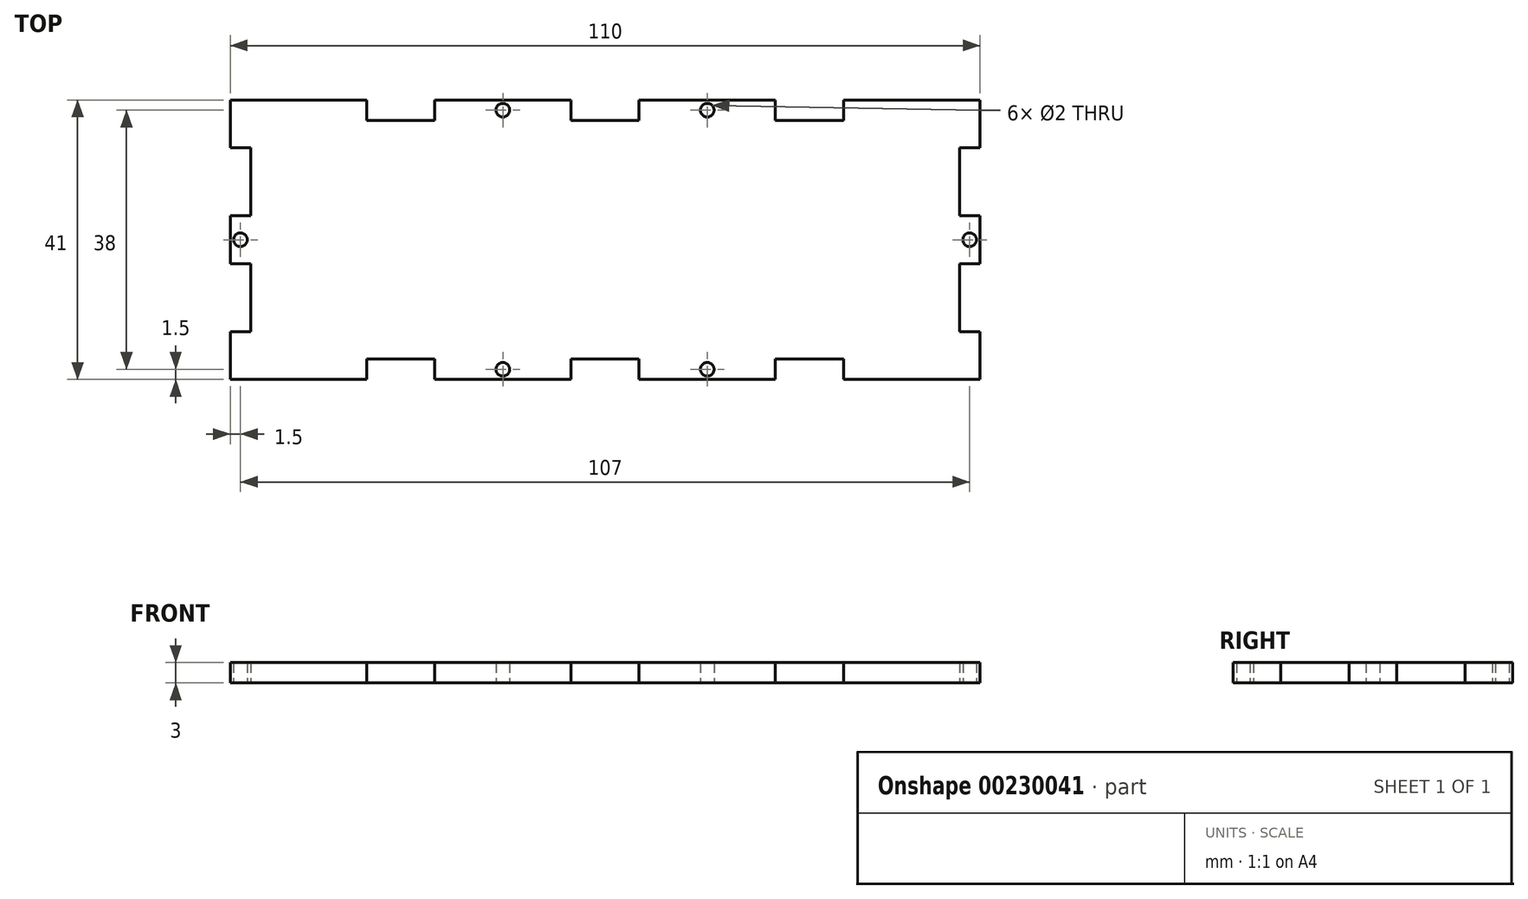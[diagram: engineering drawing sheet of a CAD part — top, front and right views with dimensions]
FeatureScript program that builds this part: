
annotation { "Feature Type Name" : "Feature", "Feature Type Description" : "" }
export const myFeature = defineFeature(function(context is Context, id is Id, definition is map)
    precondition{}
    {
        {
            var Q0;
            Q0=qCreatedBy(makeId("Top.planeOp"),FACE);
            var sketch = newSketch(context, id + "F0", { "sketchPlane" : qUnion([Q0])});
            skLineSegment(sketch, "E0", {"start": v(0, 0) * mm, "end": v(0, 7) * mm});
            skLineSegment(sketch, "E1", {"start": v(0, 7) * mm, "end": v(3, 7) * mm});
            skLineSegment(sketch, "E2", {"start": v(3, 7) * mm, "end": v(3, 17) * mm});
            skLineSegment(sketch, "E3", {"start": v(3, 17) * mm, "end": v(0, 17) * mm});
            skLineSegment(sketch, "E4", {"start": v(0, 17) * mm, "end": v(0, 24) * mm});
            skLineSegment(sketch, "E5", {"start": v(0, 24) * mm, "end": v(3, 24) * mm});
            skLineSegment(sketch, "E6", {"start": v(3, 24) * mm, "end": v(3, 34) * mm});
            skLineSegment(sketch, "E7", {"start": v(3, 34) * mm, "end": v(0, 34) * mm});
            skLineSegment(sketch, "E8", {"start": v(0, 34) * mm, "end": v(0, 41) * mm});
            skLineSegment(sketch, "E9", {"start": v(55, 41) * mm, "end": v(55, 0) * mm, "construction": true});
            skLineSegment(sketch, "E10", {"start": v(0, 20.5) * mm, "end": v(55, 20.5) * mm, "construction": true});
            skLineSegment(sketch, "E11", {"start": v(0, 41) * mm, "end": v(20, 41) * mm});
            skLineSegment(sketch, "E12", {"start": v(20, 41) * mm, "end": v(20, 38) * mm});
            skLineSegment(sketch, "E13", {"start": v(20, 38) * mm, "end": v(30, 38) * mm});
            skLineSegment(sketch, "E14", {"start": v(30, 38) * mm, "end": v(30, 41) * mm});
            skLineSegment(sketch, "E15", {"start": v(30, 41) * mm, "end": v(50, 41) * mm});
            skLineSegment(sketch, "E16", {"start": v(50, 41) * mm, "end": v(50, 38) * mm});
            skLineSegment(sketch, "E17", {"start": v(50, 38) * mm, "end": v(55, 38) * mm});
            skLineSegment(sketch, "E18.MirrorCS", {"start": v(3, 7) * mm, "end": v(0, 7) * mm});
            skLineSegment(sketch, "E19.MirrorCS", {"start": v(0, 7) * mm, "end": v(0, 0) * mm});
            skLineSegment(sketch, "E20.MirrorCS", {"start": v(0, 0) * mm, "end": v(20, 0) * mm});
            skLineSegment(sketch, "E21.MirrorCS", {"start": v(30, 0) * mm, "end": v(50, 0) * mm});
            skLineSegment(sketch, "E22.MirrorCS", {"start": v(30, 3) * mm, "end": v(30, 0) * mm});
            skLineSegment(sketch, "E23.MirrorCS", {"start": v(50, 0) * mm, "end": v(50, 3) * mm});
            skLineSegment(sketch, "E24.MirrorCS", {"start": v(50, 3) * mm, "end": v(55, 3) * mm});
            skLineSegment(sketch, "E25.MirrorCS", {"start": v(20, 0) * mm, "end": v(20, 3) * mm});
            skLineSegment(sketch, "E26.MirrorCS", {"start": v(20, 3) * mm, "end": v(30, 3) * mm});
            skCircle(sketch, "E27", {"center": v(40, 39.5) * mm, "radius": 1 * mm});
            skPoint(sketch, "E27.centerSnap0", {"position": v(50, 39.5) * mm});
            skPoint(sketch, "E27.centerSnap1", {"position": v(40, 41) * mm});
            skCircle(sketch, "E28.MirrorC", {"center": v(40, 1.5) * mm, "radius": 1 * mm});
            skLineSegment(sketch, "E29.MirrorCS", {"start": v(110, 7) * mm, "end": v(107, 7) * mm});
            skLineSegment(sketch, "E30.MirrorCS", {"start": v(107, 7) * mm, "end": v(110, 7) * mm});
            skLineSegment(sketch, "E31.MirrorCS", {"start": v(107, 17) * mm, "end": v(110, 17) * mm});
            skLineSegment(sketch, "E32.MirrorCS", {"start": v(110, 24) * mm, "end": v(107, 24) * mm});
            skLineSegment(sketch, "E33.MirrorCS", {"start": v(107, 34) * mm, "end": v(110, 34) * mm});
            skLineSegment(sketch, "E34.MirrorCS", {"start": v(90, 0) * mm, "end": v(90, 3) * mm});
            skLineSegment(sketch, "E35.MirrorCS", {"start": v(60, 0) * mm, "end": v(60, 3) * mm});
            skLineSegment(sketch, "E36.MirrorCS", {"start": v(80, 3) * mm, "end": v(80, 0) * mm});
            skLineSegment(sketch, "E37.MirrorCS", {"start": v(60, 41) * mm, "end": v(60, 38) * mm});
            skLineSegment(sketch, "E38.MirrorCS", {"start": v(110, 7) * mm, "end": v(110, 0) * mm});
            skCircle(sketch, "E39.MirrorC", {"center": v(70, 39.5) * mm, "radius": 1 * mm});
            skPoint(sketch, "E40.MirrorP", {"position": v(60, 39.5) * mm});
            skCircle(sketch, "E41.MirrorC", {"center": v(70, 1.5) * mm, "radius": 1 * mm});
            skLineSegment(sketch, "E42.MirrorCS", {"start": v(90, 3) * mm, "end": v(80, 3) * mm});
            skLineSegment(sketch, "E43.MirrorCS", {"start": v(60, 3) * mm, "end": v(55, 3) * mm});
            skLineSegment(sketch, "E44.MirrorCS", {"start": v(80, 0) * mm, "end": v(60, 0) * mm});
            skLineSegment(sketch, "E45.MirrorCS", {"start": v(90, 38) * mm, "end": v(80, 38) * mm});
            skLineSegment(sketch, "E46.MirrorCS", {"start": v(60, 38) * mm, "end": v(55, 38) * mm});
            skLineSegment(sketch, "E47.MirrorCS", {"start": v(80, 38) * mm, "end": v(80, 41) * mm});
            skPoint(sketch, "E48.MirrorP", {"position": v(70, 41) * mm});
            skLineSegment(sketch, "E49.MirrorCS", {"start": v(80, 41) * mm, "end": v(60, 41) * mm});
            skLineSegment(sketch, "E50.MirrorCS", {"start": v(110, 0) * mm, "end": v(110, 7) * mm});
            skLineSegment(sketch, "E51.MirrorCS", {"start": v(107, 7) * mm, "end": v(107, 17) * mm});
            skLineSegment(sketch, "E52.MirrorCS", {"start": v(110, 17) * mm, "end": v(110, 24) * mm});
            skLineSegment(sketch, "E53.MirrorCS", {"start": v(107, 24) * mm, "end": v(107, 34) * mm});
            skLineSegment(sketch, "E54.MirrorCS", {"start": v(110, 34) * mm, "end": v(110, 41) * mm});
            skLineSegment(sketch, "E55.MirrorCS", {"start": v(110, 20.5) * mm, "end": v(55, 20.5) * mm, "construction": true});
            skLineSegment(sketch, "E56.MirrorCS", {"start": v(110, 41) * mm, "end": v(90, 41) * mm});
            skLineSegment(sketch, "E57.MirrorCS", {"start": v(90, 41) * mm, "end": v(90, 38) * mm});
            skLineSegment(sketch, "E58.MirrorCS", {"start": v(110, 0) * mm, "end": v(90, 0) * mm});
            skCircle(sketch, "E59", {"center": v(1.5, 20.5) * mm, "radius": 1 * mm});
            skPoint(sketch, "E59.centerSnap0", {"position": v(1.5, 34) * mm});
            skCircle(sketch, "E60.MirrorC", {"center": v(108.5, 20.5) * mm, "radius": 1 * mm});
            skPoint(sketch, "E61.centerSnap0", {"position": v(85, 38) * mm});
            skSolve(sketch);
        }
        {
            var Q0;
            Q0 = qSketchRegion(id + "F0", true);
            extrude(context, id + "F1", {"entities" : qUnion([Q0]), "endBound" : BoundingType.SYMMETRIC, "depth" : 3 * mm});
        }
    });
